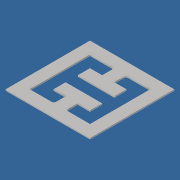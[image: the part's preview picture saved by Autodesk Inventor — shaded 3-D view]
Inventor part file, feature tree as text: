
AUTODESK INVENTOR PART (.ipt)
format: ipt  version: 2016 (Build 200138000, 138)  size: 183,808 bytes
history: native  units: in
note: dims shown in document units (in); Inventor stores cm internally (conversion verified against a paired STEP export)
features: extrude x1, sketch x1
ambient origin geometry x8: Origin, YZ Plane, XZ Plane, XY Plane, X Axis, Y Axis, Z Axis, Center Point
bodies: Solid1 (feature_tree)
feature tree (2):
  extrude  "Extrusion1"  Depth=0.673in
  sketch  "Sketch1"  dims[d0=0.01in d1=0.0in d2=0.673in]
